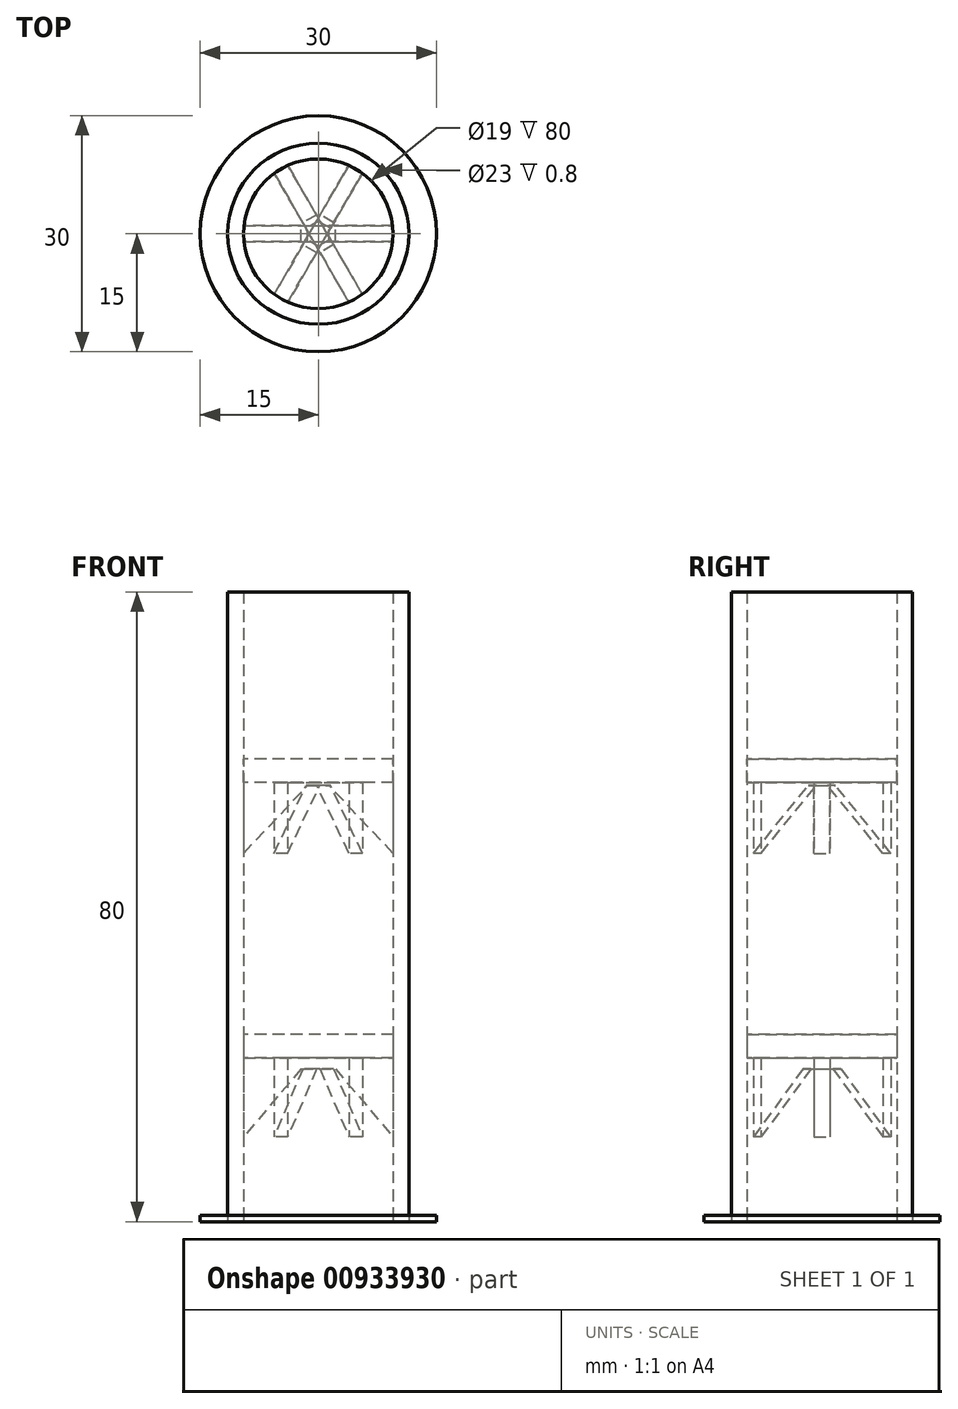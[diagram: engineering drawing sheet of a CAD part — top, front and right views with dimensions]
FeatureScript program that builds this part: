
annotation { "Feature Type Name" : "Feature", "Feature Type Description" : "" }
export const myFeature = defineFeature(function(context is Context, id is Id, definition is map)
    precondition{}
    {
        {
            var Q0;
            Q0=qCreatedBy(makeId("Top.planeOp"),FACE);
            var sketch = newSketch(context, id + "F0", { "sketchPlane" : qUnion([Q0])});
            skCircle(sketch, "E0", {"center": v(0, 0) * mm, "radius": 11.5 * mm});
            skCircle(sketch, "E1", {"center": v(0, 0) * mm, "radius": 9.5 * mm});
            skCircle(sketch, "E2", {"center": v(0, 0) * mm, "radius": 15 * mm});
            skSolve(sketch);
        }
        {
            var Q0;
            Q0=makeQuery(id+"F0.imprint","IMPRINT",FACE,{"disambiguationData":[TD([[makeQuery(id+"F0.imprint","IMPRINT",EDGE,{"derivedFrom":sQuery(id+"F0.wireOp",EDGE,"E0")}),-1.0]])]});
            var Q1;
            Q1=makeQuery(id+"F0.imprint","IMPRINT",FACE,{"disambiguationData":[TD([[makeQuery(id+"F0.imprint","IMPRINT",EDGE,{"derivedFrom":sQuery(id+"F0.wireOp",EDGE,"E1")}),1.0]])]});
            extrude(context, id + "F1", {"entities" : qUnion([Q0, Q1]), "depth" : 0.8 * mm, "offsetDistance" : 25 * mm});
        }
        {
            var Q0;
            Q0=makeQuery(id+"F0.imprint","IMPRINT",FACE,{"disambiguationData":[TD([[makeQuery(id+"F0.imprint","IMPRINT",EDGE,{"derivedFrom":sQuery(id+"F0.wireOp",EDGE,"E0")}),1.0]])]});
            extrude(context, id + "F2", {"entities" : qUnion([Q0]), "depth" : 80 * mm, "offsetDistance" : 25 * mm});
        }
        {
            var Q0;
            Q0=makeQuery(id+"F1.opExtrude","CAP_FACE",FACE,{"disambiguationData":[OSD([sQuery(id+"F0.wireOp",EDGE,"E1")])],"isStart":false});
            cPlane(context, id + "F3", {"entities" : qUnion([Q0]), "cplaneType" : CPlaneType.OFFSET, "offset" : 20 * mm, "width" : 150 * mm, "height" : 150 * mm});
        }
        {
            var Q0;
            Q0=qCreatedBy(id+"F3.planeOp",FACE);
            var sketch = newSketch(context, id + "F4", { "sketchPlane" : qUnion([Q0])});
            skCircle(sketch, "E3", {"center": v(0, 0) * mm, "radius": 9.5 * mm});
            skSolve(sketch);
        }
        {
            var Q0;
            Q0=makeQuery(id+"F4.imprint","IMPRINT",FACE,{"disambiguationData":[TD([[makeQuery(id+"F4.imprint","IMPRINT",EDGE,{"derivedFrom":sQuery(id+"F4.wireOp",EDGE,"E3")}),1.0]])]});
            extrude(context, id + "F5", {"entities" : qUnion([Q0]), "depth" : 3 * mm, "offsetDistance" : 25 * mm});
        }
        {
            var Q0;
            Q0=makeQuery(id+"F5.opExtrude","CAP_FACE",FACE,{"disambiguationData":[OSD([sQuery(id+"F4.wireOp",EDGE,"E3")])],"isStart":false});
            cPlane(context, id + "F6", {"entities" : qUnion([Q0]), "cplaneType" : CPlaneType.OFFSET, "offset" : 35 * mm, "width" : 150 * mm, "height" : 150 * mm});
        }
        {
            var Q0;
            Q0=qCreatedBy(id+"F6.planeOp",FACE);
            var sketch = newSketch(context, id + "F7", { "sketchPlane" : qUnion([Q0])});
            skCircle(sketch, "E4", {"center": v(0, 0) * mm, "radius": 9.5 * mm});
            skSolve(sketch);
        }
        {
            var Q0;
            Q0=makeQuery(id+"F7.imprint","IMPRINT",FACE,{"disambiguationData":[TD([[makeQuery(id+"F7.imprint","IMPRINT",EDGE,{"derivedFrom":sQuery(id+"F7.wireOp",EDGE,"E4")}),1.0]])]});
            extrude(context, id + "F8", {"entities" : qUnion([Q0]), "oppositeDirection" : true, "depth" : 3 * mm, "offsetDistance" : 25 * mm});
        }
        {
            var Q0;
            Q0=qCreatedBy(makeId("Front.planeOp"),FACE);
            var sketch = newSketch(context, id + "F9", { "sketchPlane" : qUnion([Q0])});
            skLineSegment(sketch, "E5", {"start": v(0, 0) * mm, "end": v(-9.5, 0) * mm, "construction": true});
            skLineSegment(sketch, "E6", {"start": v(-9.5, 0) * mm, "end": v(-9.5, 0.8) * mm, "construction": true});
            skLineSegment(sketch, "E7", {"start": v(0, 0) * mm, "end": v(0, 100) * mm, "construction": true});
            skLineSegment(sketch, "E8", {"start": v(-9.5, 20.8) * mm, "end": v(-1, 20.8) * mm});
            skLineSegment(sketch, "E9", {"start": v(-1, 20.8) * mm, "end": v(-9.5, 10.76) * mm});
            skLineSegment(sketch, "E10", {"start": v(-9.5, 20.8) * mm, "end": v(-9.5, 10.76) * mm});
            skLineSegment(sketch, "E11.MirrorCS", {"start": v(1, 20.8) * mm, "end": v(9.5, 10.76) * mm});
            skLineSegment(sketch, "E12.MirrorCS", {"start": v(9.5, 20.8) * mm, "end": v(1, 20.8) * mm});
            skLineSegment(sketch, "E13.MirrorCS", {"start": v(9.5, 20.8) * mm, "end": v(9.5, 10.76) * mm});
            skLineSegment(sketch, "E14", {"start": v(0, 0) * mm, "end": v(0, 0.8) * mm, "construction": true});
            skLineSegment(sketch, "E15", {"start": v(0, 0.8) * mm, "end": v(0, 20.8) * mm, "construction": true});
            skLineSegment(sketch, "E16", {"start": v(0, 20.8) * mm, "end": v(0, 23.8) * mm, "construction": true});
            skLineSegment(sketch, "E17", {"start": v(0, 23.8) * mm, "end": v(0, 55.8) * mm, "construction": true});
            skLineSegment(sketch, "E18", {"start": v(0, 20.8) * mm, "end": v(-1, 20.8) * mm, "construction": true});
            skLineSegment(sketch, "E19", {"start": v(0, 55.8) * mm, "end": v(-1, 55.8) * mm, "construction": true});
            skLineSegment(sketch, "E20", {"start": v(-1, 55.8) * mm, "end": v(-9.5, 55.8) * mm});
            skLineSegment(sketch, "E21", {"start": v(-9.5, 55.8) * mm, "end": v(-9.5, 46.8) * mm});
            skLineSegment(sketch, "E22", {"start": v(-9.5, 46.8) * mm, "end": v(-1, 55.8) * mm});
            skLineSegment(sketch, "E23.MirrorCS", {"start": v(9.5, 55.8) * mm, "end": v(9.5, 46.8) * mm});
            skLineSegment(sketch, "E24.MirrorCS", {"start": v(9.5, 46.8) * mm, "end": v(1, 55.8) * mm});
            skLineSegment(sketch, "E25.MirrorCS", {"start": v(1, 55.8) * mm, "end": v(9.5, 55.8) * mm});
            skLineSegment(sketch, "E26", {"start": v(-1, 20.8) * mm, "end": v(0, 20.8) * mm});
            skLineSegment(sketch, "E27", {"start": v(-2.19, 19.4) * mm, "end": v(0, 19.4) * mm});
            skLineSegment(sketch, "E28.MirrorCS", {"start": v(1, 20.8) * mm, "end": v(0, 20.8) * mm});
            skLineSegment(sketch, "E29.MirrorCS", {"start": v(0, 20.8) * mm, "end": v(1, 20.8) * mm, "construction": true});
            skLineSegment(sketch, "E30.MirrorCS", {"start": v(2.19, 19.4) * mm, "end": v(0, 19.4) * mm});
            skLineSegment(sketch, "E31", {"start": v(-1, 55.8) * mm, "end": v(0, 55.8) * mm});
            skLineSegment(sketch, "E32", {"start": v(-1.38, 55.4) * mm, "end": v(0, 55.4) * mm});
            skLineSegment(sketch, "E33.MirrorCS", {"start": v(1, 55.8) * mm, "end": v(0, 55.8) * mm});
            skLineSegment(sketch, "E34.MirrorCS", {"start": v(1.38, 55.4) * mm, "end": v(0, 55.4) * mm});
            skLineSegment(sketch, "E35.MirrorCS", {"start": v(0, 55.8) * mm, "end": v(1, 55.8) * mm, "construction": true});
            skSolve(sketch);
        }
        {
            var Q0;
            Q0 = qSketchRegion(id + "F9", true);
            extrude(context, id + "F10", {"entities" : qUnion([Q0]), "endBound" : BoundingType.SYMMETRIC, "depth" : 2 * mm, "offsetDistance" : 25 * mm});
        }
        {
            var Q0;
            Q0=makeQuery(id+"F10.opExtrude","SWEPT_BODY",BODY,{"disambiguationData":[OSD([sQuery(id+"F9.wireOp",EDGE,"E8"),sQuery(id+"F9.wireOp",EDGE,"E9"),sQuery(id+"F9.wireOp",EDGE,"E10"),sQuery(id+"F9.wireOp",EDGE,"E11.MirrorCS"),sQuery(id+"F9.wireOp",EDGE,"E12.MirrorCS"),sQuery(id+"F9.wireOp",EDGE,"E13.MirrorCS"),sQuery(id+"F9.wireOp",EDGE,"E26"),sQuery(id+"F9.wireOp",EDGE,"E27"),sQuery(id+"F9.wireOp",EDGE,"E28.MirrorCS"),sQuery(id+"F9.wireOp",EDGE,"E30.MirrorCS")])]});
            var Q1;
            Q1=makeQuery(id+"F10.opExtrude","SWEPT_BODY",BODY,{"disambiguationData":[OSD([sQuery(id+"F9.wireOp",EDGE,"E20"),sQuery(id+"F9.wireOp",EDGE,"E21"),sQuery(id+"F9.wireOp",EDGE,"E22"),sQuery(id+"F9.wireOp",EDGE,"E23.MirrorCS"),sQuery(id+"F9.wireOp",EDGE,"E24.MirrorCS"),sQuery(id+"F9.wireOp",EDGE,"E25.MirrorCS"),sQuery(id+"F9.wireOp",EDGE,"E31"),sQuery(id+"F9.wireOp",EDGE,"E32"),sQuery(id+"F9.wireOp",EDGE,"E33.MirrorCS"),sQuery(id+"F9.wireOp",EDGE,"E34.MirrorCS")])]});
            var Q2;
            Q2=sQuery(id+"F9.wireOp",EDGE,"E7");
            circularPattern(context, id + "F11", {"entities" : qUnion([Q0, Q1]), "axis" : qUnion([Q2]), "angle" : 120 * degree, "instanceCount" : 3, "equalSpace" : true});
        }
    });
